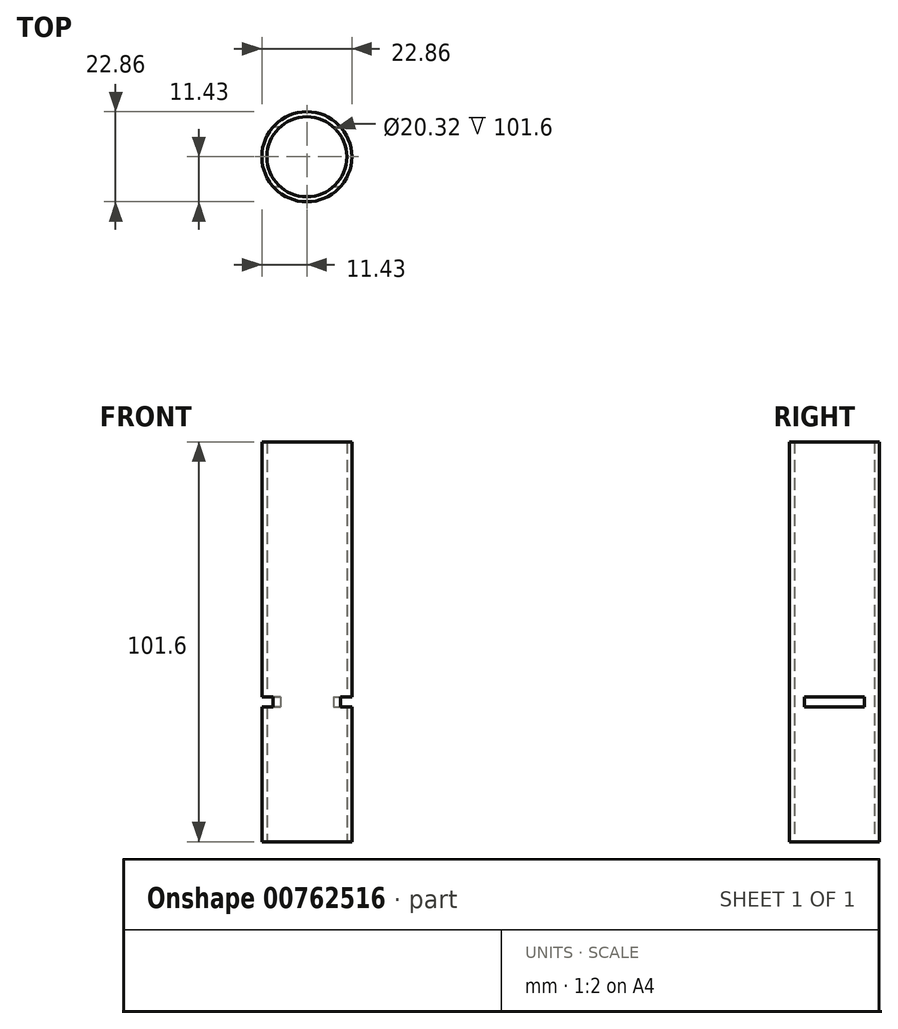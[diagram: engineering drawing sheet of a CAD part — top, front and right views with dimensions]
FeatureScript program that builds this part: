
annotation { "Feature Type Name" : "Feature", "Feature Type Description" : "" }
export const myFeature = defineFeature(function(context is Context, id is Id, definition is map)
    precondition{}
    {
        {
            var Q0;
            Q0=qCreatedBy(makeId("Top.planeOp"),FACE);
            var sketch = newSketch(context, id + "F0", { "sketchPlane" : qUnion([Q0])});
            skCircle(sketch, "E0", {"center": v(0, 0) * mm, "radius": 10.16 * mm});
            skCircle(sketch, "E1", {"center": v(0, 0) * mm, "radius": 11.43 * mm});
            skSolve(sketch);
        }
        {
            var Q0;
            Q0 = qSketchRegion(id + "F0", true);
            extrude(context, id + "F1", {"entities" : qUnion([Q0]), "depth" : 101.6 * mm, "offsetDistance" : 25.4 * mm});
        }
        {
            var Q0;
            Q0=qCreatedBy(makeId("Right.planeOp"),FACE);
            var sketch = newSketch(context, id + "F2", { "sketchPlane" : qUnion([Q0])});
            skLineSegment(sketch, "E2", {"start": v(0, 0) * mm, "end": v(0, 34.24) * mm});
            skLineSegment(sketch, "E3", {"start": v(0, 34.24) * mm, "end": v(7.62, 34.24) * mm});
            skLineSegment(sketch, "E4", {"start": v(7.62, 34.24) * mm, "end": v(7.62, 36.78) * mm});
            skLineSegment(sketch, "E5", {"start": v(7.62, 36.78) * mm, "end": v(-7.62, 36.78) * mm});
            skLineSegment(sketch, "E6", {"start": v(-7.62, 36.78) * mm, "end": v(-7.62, 34.24) * mm});
            skLineSegment(sketch, "E7", {"start": v(-7.62, 34.24) * mm, "end": v(0, 34.24) * mm});
            skSolve(sketch);
        }
        {
            var Q0;
            Q0 = qSketchRegion(id + "F2", true);
            extrude(context, id + "F3", {"entities" : qUnion([Q0]), "endBound" : BoundingType.SYMMETRIC, "oppositeDirection" : true, "depth" : 25.4 * mm, "offsetDistance" : 25.4 * mm});
        }
        {
            var Q0;
            Q0=makeQuery(id+"F3.opExtrude","SWEPT_BODY",BODY,{"disambiguationData":[OSD([sQuery(id+"F2.wireOp",EDGE,"E3"),sQuery(id+"F2.wireOp",EDGE,"E4"),sQuery(id+"F2.wireOp",EDGE,"E5"),sQuery(id+"F2.wireOp",EDGE,"E6"),sQuery(id+"F2.wireOp",EDGE,"E7")])]});
            var Q1;
            Q1=makeQuery(id+"F1.opExtrude","SWEPT_BODY",BODY,{"disambiguationData":[OSD([sQuery(id+"F0.wireOp",EDGE,"E0"),sQuery(id+"F0.wireOp",EDGE,"E1")])]});
            booleanBodies(context, id + "F4", {"operationType" : BooleanOperationType.SUBTRACTION, "tools" : qUnion([Q0]), "targets" : qUnion([Q1])});
        }
    });
